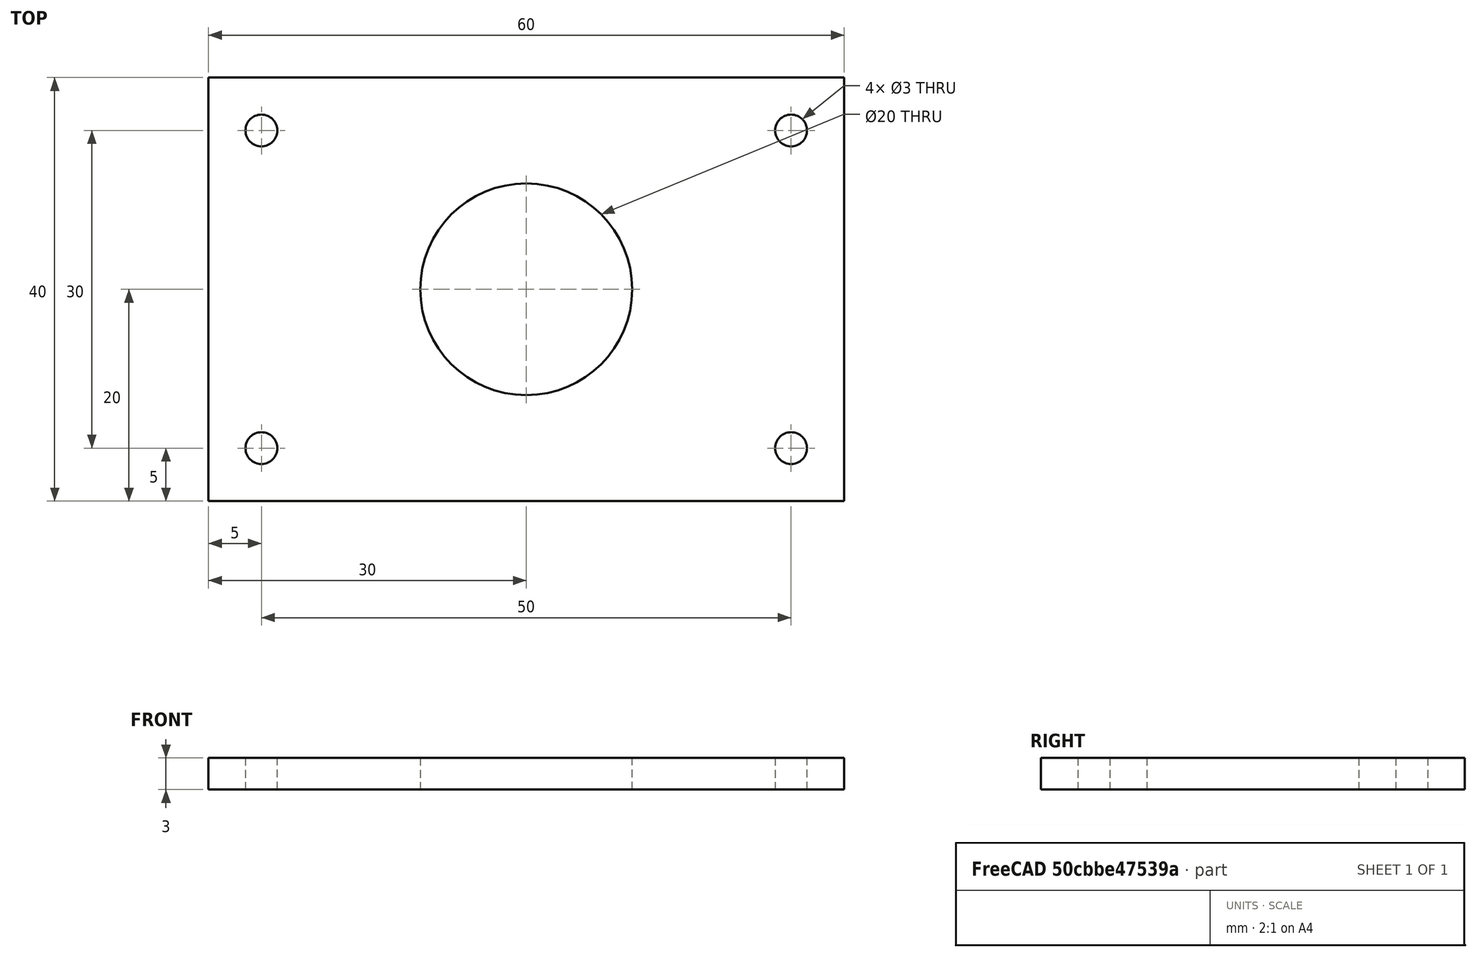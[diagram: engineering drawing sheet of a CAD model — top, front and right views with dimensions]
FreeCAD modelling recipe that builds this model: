
FCSTD DOCUMENT  (FreeCAD 0.17R13217 (Git))
Label: 08-Base-taladros
License: All rights reserved
LicenseURL: http://en.wikipedia.org/wiki/All_rights_reserved
objects: Sketcher::SketchObject×1, PartDesign::Pad×1, PartDesign::Body×1
note: 4 computed .brp shape members not serialized (recipe doc carries the construction recipe); baked Part::Feature solids carry a one-line shape summary decoded from their .brp

FEATURE [Sketcher::SketchObject] Sketch
  MapMode = 5
  Support = -> [XY_Plane]
  sketch-geometry (14):
    g0: LineSegment [constr] StartX=-25 StartY=15 StartZ=0 EndX=25 EndY=15 EndZ=0
    g1: LineSegment [constr] StartX=25 StartY=15 StartZ=0 EndX=25 EndY=-15 EndZ=0
    g2: LineSegment [constr] StartX=25 StartY=-15 StartZ=0 EndX=-25 EndY=-15 EndZ=0
    g3: LineSegment [constr] StartX=-25 StartY=-15 StartZ=0 EndX=-25 EndY=15 EndZ=0
    g4: LineSegment StartX=-30 StartY=20 StartZ=0 EndX=30 EndY=20 EndZ=0
    g5: LineSegment StartX=30 StartY=20 StartZ=0 EndX=30 EndY=-20 EndZ=0
    g6: LineSegment StartX=30 StartY=-20 StartZ=0 EndX=-30 EndY=-20 EndZ=0
    g7: LineSegment StartX=-30 StartY=-20 StartZ=0 EndX=-30 EndY=20 EndZ=0
    g8: LineSegment [constr] StartX=-30 StartY=20 StartZ=0 EndX=-25 EndY=15 EndZ=0
    g9: Circle CenterX=25 CenterY=15 CenterZ=0 NormalX=0 NormalY=0 NormalZ=1 AngleXU=0 Radius=1.5
    g10: Circle CenterX=25 CenterY=-15 CenterZ=0 NormalX=0 NormalY=0 NormalZ=1 AngleXU=0 Radius=1.5
    g11: Circle CenterX=-25 CenterY=-15 CenterZ=0 NormalX=0 NormalY=0 NormalZ=1 AngleXU=0 Radius=1.5
    g12: Circle CenterX=-25 CenterY=15 CenterZ=0 NormalX=0 NormalY=0 NormalZ=1 AngleXU=0 Radius=1.5
    g13: Circle CenterX=0 CenterY=0 CenterZ=0 NormalX=0 NormalY=0 NormalZ=1 AngleXU=0 Radius=10
  constraints (34):
    c: Coincident(g0,g1)
    c: Coincident(g1,g2)
    c: Coincident(g2,g3)
    c: Coincident(g3,g0)
    c: Horizontal(g0)
    c: Horizontal(g2)
    c: Vertical(g1)
    c: Vertical(g3)
    c: Symmetric(g0,g1,g-1)
    c: Coincident(g4,g5)
    c: Coincident(g5,g6)
    c: Coincident(g6,g7)
    c: Coincident(g7,g4)
    c: Horizontal(g4)
    c: Horizontal(g6)
    c: Vertical(g5)
    c: Vertical(g7)
    c: Symmetric(g4,g5,g-1)
    c: Coincident(g8,g4)
    c: Coincident(g8,g0)
    c: Angle(g8,g4) = 0.785398
    c: DistanceX(g4,g0) = 5
    c: Coincident(g9,g0)
    c: Coincident(g10,g1)
    c: Coincident(g11,g2)
    c: Coincident(g12,g0)
    c: Equal(g12,g11)
    c: Equal(g11,g10)
    c: Equal(g10,g9)
    c: Radius(g9) = 1.5
    c: DistanceX(g4,g4) = 60
    c: DistanceY(g5,g5) = 40
    c: Coincident(g13,g-1)
    c: Radius(g13) = 10
FEATURE [PartDesign::Pad] Pad
  Length = 3
  Length2 = 100
  Profile = -> Sketch
  Refine = true
  Type = 0
FEATURE [PartDesign::Body] Body
  Group = -> [Sketch,Pad]
  Origin = -> Origin
  Tip = -> Pad
